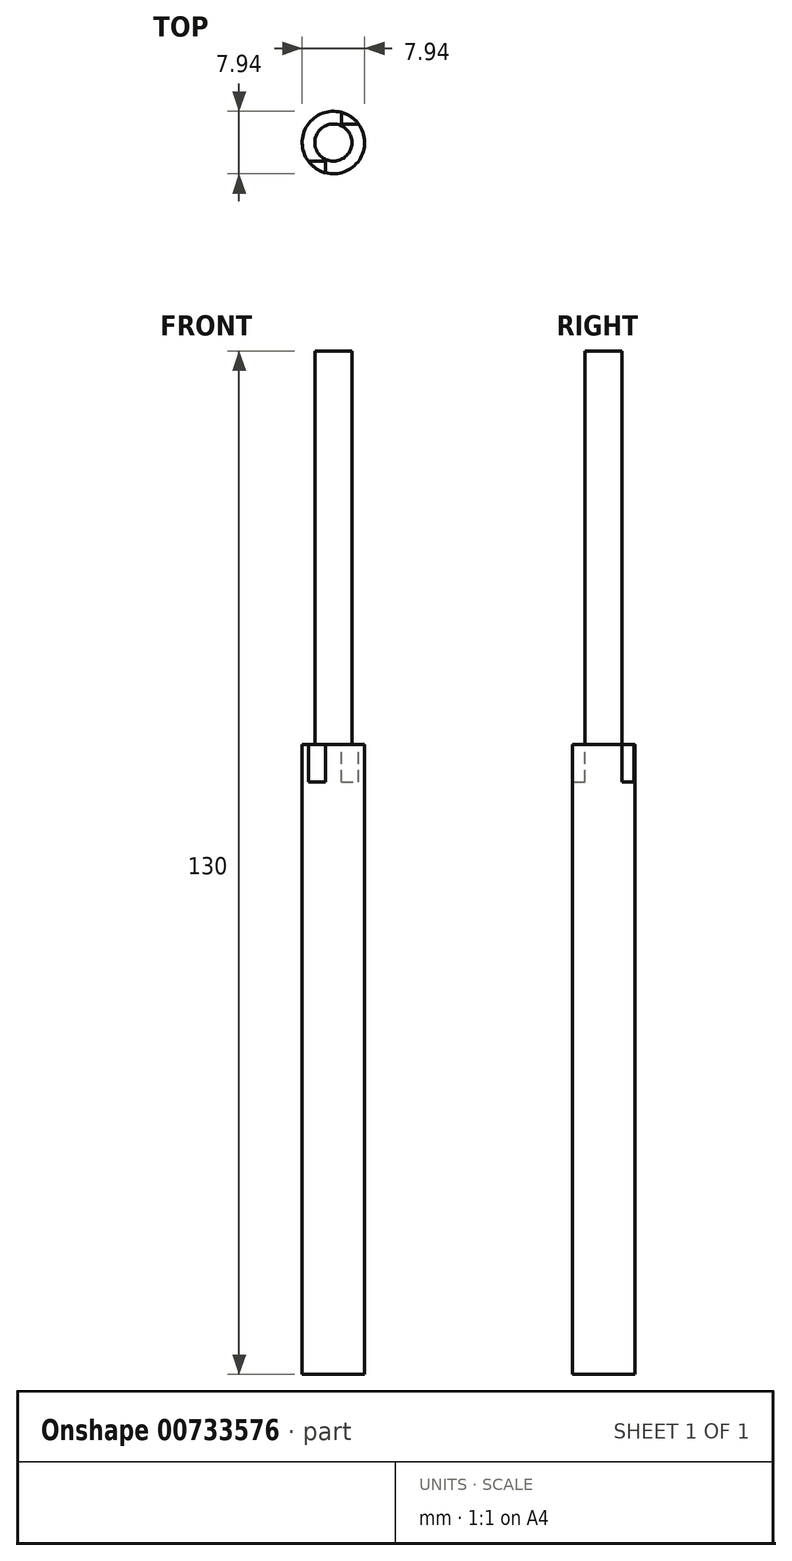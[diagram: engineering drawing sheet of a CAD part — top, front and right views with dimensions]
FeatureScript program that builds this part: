
annotation { "Feature Type Name" : "Feature", "Feature Type Description" : "" }
export const myFeature = defineFeature(function(context is Context, id is Id, definition is map)
    precondition{}
    {
        {
            var Q0;
            Q0=qCreatedBy(makeId("Top.planeOp"),FACE);
            var sketch = newSketch(context, id + "F0", { "sketchPlane" : qUnion([Q0])});
            skCircle(sketch, "E0", {"center": v(0, 0) * mm, "radius": 2.36 * mm});
            skSolve(sketch);
        }
        {
            var Q0;
            Q0 = qSketchRegion(id + "F0", true);
            extrude(context, id + "F1", {"entities" : qUnion([Q0]), "depth" : 50 * mm, "offsetDistance" : 25 * mm});
        }
        {
            var Q0;
            Q0=makeQuery(id+"F1.opExtrude","CAP_FACE",FACE,{"disambiguationData":[OSD([sQuery(id+"F0.wireOp",EDGE,"E0")])],"isStart":true});
            var sketch = newSketch(context, id + "F2", { "sketchPlane" : qUnion([Q0])});
            skCircle(sketch, "E1", {"center": v(0, 0) * mm, "radius": 3.97 * mm});
            skSolve(sketch);
        }
        {
            var Q0;
            Q0 = qSketchRegion(id + "F2", true);
            extrude(context, id + "F3", {"entities" : qUnion([Q0]), "operationType" : NewBodyOperationType.ADD, "depth" : 80 * mm, "offsetDistance" : 25 * mm});
        }
        {
            var Q0;
            Q0=makeQuery(id+"F3.opExtrude","CAP_FACE",FACE,{"disambiguationData":[OSD([sQuery(id+"F2.wireOp",EDGE,"E1")])],"isStart":true});
            var sketch = newSketch(context, id + "F4", { "sketchPlane" : qUnion([Q0])});
            skLineSegment(sketch, "E2.bottom", {"start": v(1, -3.84) * mm, "end": v(-1, -3.84) * mm});
            skLineSegment(sketch, "E2.top", {"start": v(1, 3.84) * mm, "end": v(-1, 3.84) * mm});
            skLineSegment(sketch, "E2.left", {"start": v(1, -3.84) * mm, "end": v(1, 3.84) * mm});
            skLineSegment(sketch, "E2.right", {"start": v(-1, -3.84) * mm, "end": v(-1, 3.84) * mm});
            skPoint(sketch, "E2.middle", {"position": v(0, 0) * mm});
            skLineSegment(sketch, "E3.bottom", {"start": v(0, -2.36) * mm, "end": v(-4.16, -2.36) * mm});
            skLineSegment(sketch, "E3.top", {"start": v(0, -3.84) * mm, "end": v(-4.16, -3.84) * mm});
            skLineSegment(sketch, "E3.left", {"start": v(0, -2.36) * mm, "end": v(0, -3.84) * mm});
            skLineSegment(sketch, "E3.right", {"start": v(-4.16, -2.36) * mm, "end": v(-4.16, -3.84) * mm});
            skLineSegment(sketch, "E4.bottom", {"start": v(0, 2.36) * mm, "end": v(4.81, 2.36) * mm});
            skLineSegment(sketch, "E4.top", {"start": v(0, 3.84) * mm, "end": v(4.81, 3.84) * mm});
            skLineSegment(sketch, "E4.left", {"start": v(0, 2.36) * mm, "end": v(0, 3.84) * mm});
            skLineSegment(sketch, "E4.right", {"start": v(4.81, 2.36) * mm, "end": v(4.81, 3.84) * mm});
            skSolve(sketch);
        }
        {
            var Q0;
            {var subQ0=sQuery(id+"F4.wireOp",EDGE,"E2.left");var subQ3=makeQuery(id+"F1.opExtrude","CAP_EDGE",EDGE,{"disambiguationData":[OSD([sQuery(id+"F0.wireOp",EDGE,"E0")])],"isStart":true});var subQ4=makeQuery(id+"F4.imprint","INTERSECT",VERTEX,{"disambiguationData":[OD(0.0)],"derivedFrom":[subQ3,subQ0]});Q0=makeQuery(id+"F4.imprint","IMPRINT",FACE,{"disambiguationData":[TD([[makeQuery(id+"F4.imprint","IMPRINT",EDGE,{"disambiguationData":[TD([[subQ4,-1.0]])],"derivedFrom":subQ3}),-1.0]])]});}
            var sketch = newSketch(context, id + "F5", { "sketchPlane" : qUnion([Q0])});
            skSolve(sketch);
        }
        {
            var Q0;
            {var subQ0=sQuery(id+"F4.wireOp",EDGE,"E2.left");var subQ3=makeQuery(id+"F1.opExtrude","CAP_EDGE",EDGE,{"disambiguationData":[OSD([sQuery(id+"F0.wireOp",EDGE,"E0")])],"isStart":true});var subQ4=makeQuery(id+"F4.imprint","INTERSECT",VERTEX,{"disambiguationData":[OD(0.0)],"derivedFrom":[subQ3,subQ0]});Q0=makeQuery(id+"F5.imprint","IMPRINT",FACE,{"disambiguationData":[TD([[makeQuery(id+"F5.imprint","IMPRINT",EDGE,{"derivedFrom":makeQuery(id+"F4.imprint","IMPRINT",EDGE,{"disambiguationData":[TD([[subQ4,-1.0]])],"derivedFrom":subQ3})}),-1.0]])]});}
            var sketch = newSketch(context, id + "F6", { "sketchPlane" : qUnion([Q0])});
            skSolve(sketch);
        }
        {
            var Q0;
            {var subQ0=sQuery(id+"F4.wireOp",EDGE,"E2.left");var subQ3=sQuery(id+"F4.wireOp",EDGE,"E4.bottom");var subQ4=makeQuery(id+"F4.imprint","INTERSECT",VERTEX,{"derivedFrom":[subQ0,subQ3]});Q0=makeQuery(id+"F4.imprint","IMPRINT",FACE,{"disambiguationData":[TD([[makeQuery(id+"F4.imprint","IMPRINT",EDGE,{"disambiguationData":[TD([[subQ4,-1.0]])],"derivedFrom":subQ3}),1.0]])]});}
            var Q1;
            {var subQ0=sQuery(id+"F4.wireOp",EDGE,"E2.right");var subQ3=sQuery(id+"F4.wireOp",EDGE,"E3.bottom");var subQ4=makeQuery(id+"F4.imprint","INTERSECT",VERTEX,{"derivedFrom":[subQ0,subQ3]});Q1=makeQuery(id+"F4.imprint","IMPRINT",FACE,{"disambiguationData":[TD([[makeQuery(id+"F4.imprint","IMPRINT",EDGE,{"disambiguationData":[TD([[subQ4,-1.0]])],"derivedFrom":subQ3}),1.0]])]});}
            extrude(context, id + "F7", {"entities" : qUnion([Q0, Q1]), "operationType" : NewBodyOperationType.REMOVE, "oppositeDirection" : true, "depth" : 4.76 * mm, "offsetDistance" : 25 * mm});
        }
    });
